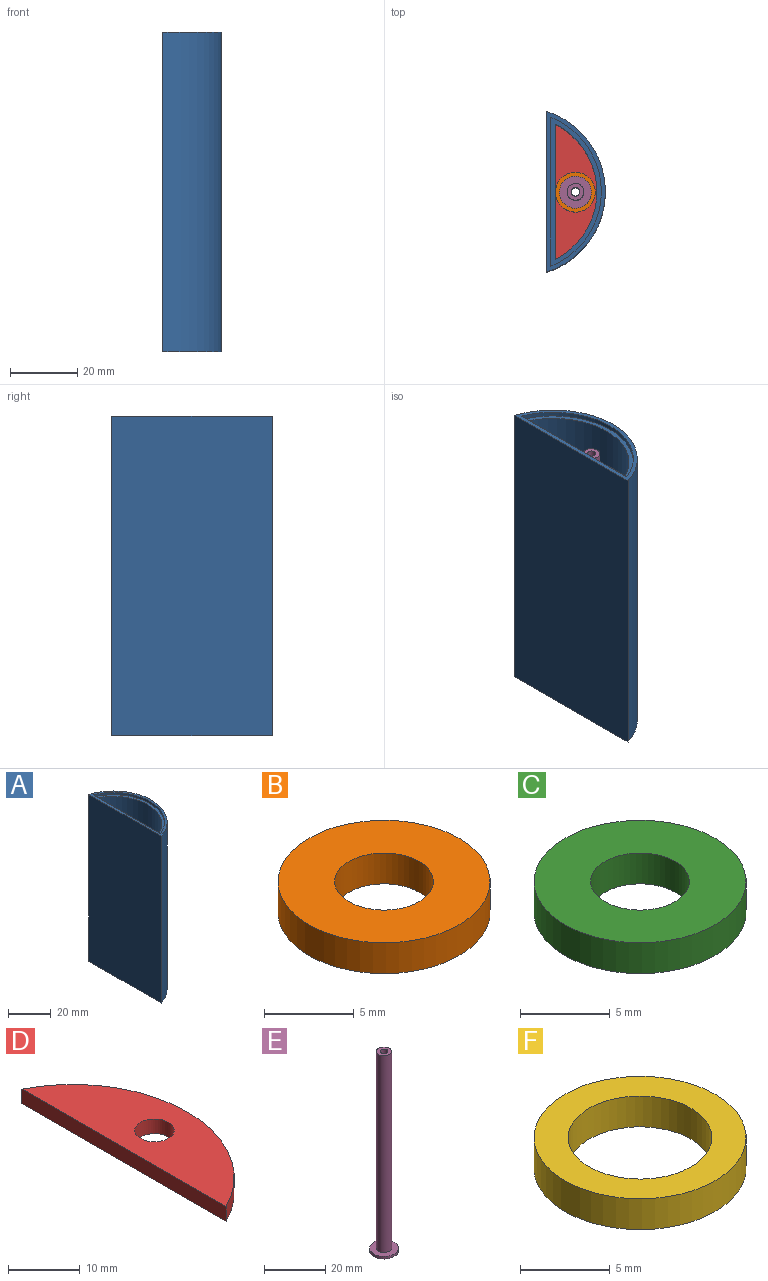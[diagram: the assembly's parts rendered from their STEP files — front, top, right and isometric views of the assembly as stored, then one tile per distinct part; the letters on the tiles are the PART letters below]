
ASSEMBLY  parts=6 mates=5
PART A: 9 faces, bbox 17.4x47.6x95 mm
  f0: cylinder r=23.8mm len=44.23mm, axis (0,0,-1), area 73.8mm2, adj f3,f4,f8
  f1: plane 95x47.63mm, normal (-1,0,0), area 4525.2mm2, adj f2,f4,f5
  f2: cylinder r=25mm len=95mm, axis (0,0,-1), area 5994.1mm2, adj f1,f4,f5
  f3: plane 44.23x1.3mm, normal (1,0,0), area 57.5mm2, adj f0,f4,f8
  f4: plane 47.63x17.4mm, normal (0,0,1), area 127.1mm2, adj f0,f1,f2,f3
  f5: plane 47.63x17.4mm, normal (0,0,-1), area 251.2mm2, adj f1,f2,f6,f7
  f6: cylinder r=22.5mm len=93.7mm, axis (0,0,-1), area 4660.4mm2, adj f5,f7,f8
  f7: plane 93.7x40.21mm, normal (1,0,0), area 3767.8mm2, adj f5,f6,f8
  f8: plane 44.23x15mm, normal (0,0,1), area 124.2mm2, adj f0,f3,f6,f7
PART B: 4 faces, bbox 11.8x11.8x2.1 mm
  f0: cylinder r=2.75mm len=5.5mm, axis (0,0,-1), area 36.3mm2, adj f2,f3
  f1: cylinder r=5.9mm len=11.8mm, axis (0,0,-1), area 77.8mm2, adj f2,f3
  f2: plane 11.8x11.8mm, normal (0,0,1), area 85.6mm2, adj f0,f1
  f3: plane 11.8x11.8mm, normal (0,0,-1), area 85.6mm2, adj f0,f1
PART C: 4 faces, bbox 11.8x11.8x2.1 mm
  f0: cylinder r=2.75mm len=5.5mm, axis (0,0,-1), area 36.3mm2, adj f2,f3
  f1: cylinder r=5.9mm len=11.8mm, axis (0,0,-1), area 77.8mm2, adj f2,f3
  f2: plane 11.8x11.8mm, normal (0,0,1), area 85.6mm2, adj f0,f1
  f3: plane 11.8x11.8mm, normal (0,0,-1), area 85.6mm2, adj f0,f1
PART D: 5 faces, bbox 12.4x40.2x2.5 mm
  f0: plane 40.21x2.5mm, normal (-1,0,0), area 100.5mm2, adj f2,f3,f4
  f1: cylinder r=2.75mm len=5.5mm, axis (0,0,-1), area 43.2mm2, adj f3,f4
  f2: cylinder r=22.5mm len=40.21mm, axis (0,0,-1), area 124.3mm2, adj f0,f3,f4
  f3: plane 40.21x12.4mm, normal (0,0,1), area 332.7mm2, adj f0,f1,f2
  f4: plane 40.21x12.4mm, normal (0,0,-1), area 332.7mm2, adj f0,f1,f2
PART E: 6 faces, bbox 9.5x9.5x80 mm
  f0: cylinder r=4.75mm len=9.5mm, axis (0,0,-1), area 29.8mm2, adj f1,f2
  f1: plane 9.5x9.5mm, normal (0,0,1), area 51.2mm2, adj f0,f4
  f2: plane 9.5x9.5mm, normal (0,0,-1), area 65.6mm2, adj f0,f3
  f3: cylinder r=1.3mm len=80mm, axis (0,0,-1), area 653.5mm2, adj f2,f5
  f4: cylinder r=2.5mm len=79mm, axis (0,0,-1), area 1240.9mm2, adj f1,f5
  f5: plane 5x5mm, normal (0,0,1), area 14.3mm2, adj f3,f4
PART F: 4 faces, bbox 11.8x11.8x2.1 mm
  f0: cylinder r=4mm len=8mm, axis (0,0,-1), area 52.8mm2, adj f2,f3
  f1: cylinder r=5.9mm len=11.8mm, axis (0,0,-1), area 77.8mm2, adj f2,f3
  f2: plane 11.8x11.8mm, normal (0,0,1), area 59.1mm2, adj f0,f1
  f3: plane 11.8x11.8mm, normal (0,0,-1), area 59.1mm2, adj f0,f1
PLACE A t=(-17.17,-0.31,-1.66)mm
PLACE B t=(-21.72,-0.31,5.04)mm
PLACE C t=(-1.07,-0.31,0.84)mm
PLACE D t=(-17.17,-0.31,-1.66)mm
PLACE E t=(-1.07,-0.31,7.14)mm
PLACE F t=(19.99,-0.31,2.94)mm
MATE fastened B.f0 <-> F.f0  axis (0,0,-1) through (-1.07,-0.31,5.04)mm
MATE fastened E.f0 <-> B.f0  axis (0,0,-1) through (-1.07,-0.31,7.14)mm
MATE fastened C.f0 <-> D.f1  axis (0,0,-1) through (-1.07,-0.31,0.84)mm
MATE fastened A.f5 <-> D.f4  axis (0,0,-1) through (-7.07,-20.42,-1.66)mm
MATE fastened F.f0 <-> C.f1  axis (0,0,-1) through (-1.07,-0.31,2.94)mm
